# Revit family: LVSKEY
name_source: partatom
category: Communication Devices
units: mm (PartAtom-declared; Revit-internal decimal feet)

## family parameters
Cut with Voids When Loaded = No
Host = Face
Maintain Annotation Orientation = No
OmniClass Number = 23.85.80.11.27
OmniClass Title = Lighting Controls
Part Type = Normal
Room Calculation Point = No
Round Connector Dimension = Use Diameter
Shared = Yes

## types (1)
- LVSKEY
    Assembly Code = D5090
    Default Elevation = 48 "
    Description = The Control Solutions' Low Voltage Heavy Duty Key Switch is
designed to provide a secure means to manually control lighting in
areas where security or access control are a concern. The center loaded
key action provides an ON with a firm twist of the key to the right and
an OFF with a twist to the left. The key can be removed in the center
position only.
    Environmental Conditions = Indoor Use only, Relative Humidity(Non Condensing) 10%-90%
    Feartures = Attractive brushed stainless steel finish
• Mounts to standard single gang switch box (not provided)
• Connect to NXCI Contact Interface Module (order separately) for CAT5
digital connection to NX Smart Port
• Low voltage Class 2 device
• Connect directly to CX or NX lighting control panels
• Tactile response for ON/OFF contacts
• Provided with two keys
    Housing Material = Metal-Galvanized_Steel
    Manufacturer = NX Lighting Controls
    Model = LVKEY
    Type Comments = Heavy Duty Key Switch
    URL = https://www.currentlighting.com
    Warranty = 5-Years Warranty

## geometry (parser evidence)
native form markers: Sweep x3
no freeform markers — native parametric forms only
